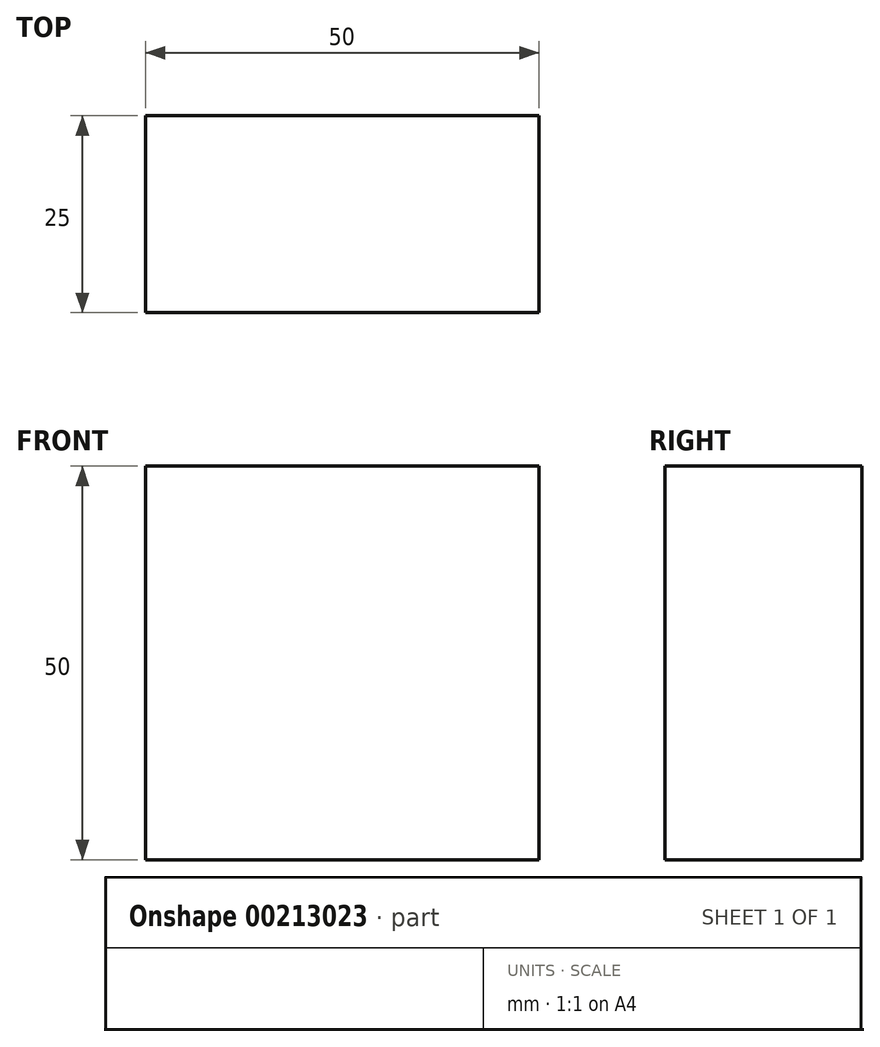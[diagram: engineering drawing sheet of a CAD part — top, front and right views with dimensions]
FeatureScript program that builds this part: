
annotation { "Feature Type Name" : "Feature", "Feature Type Description" : "" }
export const myFeature = defineFeature(function(context is Context, id is Id, definition is map)
    precondition{}
    {
        {
            var Q0;
            Q0=qCreatedBy(makeId("Front.planeOp"),FACE);
            var sketch = newSketch(context, id + "F0", { "sketchPlane" : qUnion([Q0])});
            skLineSegment(sketch, "E0.bottom", {"start": v(0, 0) * mm, "end": v(50, 0) * mm});
            skLineSegment(sketch, "E0.top", {"start": v(0, 50) * mm, "end": v(50, 50) * mm});
            skLineSegment(sketch, "E0.left", {"start": v(0, 0) * mm, "end": v(0, 50) * mm});
            skLineSegment(sketch, "E0.right", {"start": v(50, 0) * mm, "end": v(50, 50) * mm});
            skSolve(sketch);
        }
        {
            var Q0;
            Q0=makeQuery(id+"F0.imprint","IMPRINT",FACE,{"disambiguationData":[TD([[makeQuery(id+"F0.imprint","IMPRINT",EDGE,{"derivedFrom":sQuery(id+"F0.wireOp",EDGE,"E0.bottom")}),1.0]])]});
            extrude(context, id + "F1", {"entities" : qUnion([Q0]), "depth" : 25 * mm});
        }
    });
